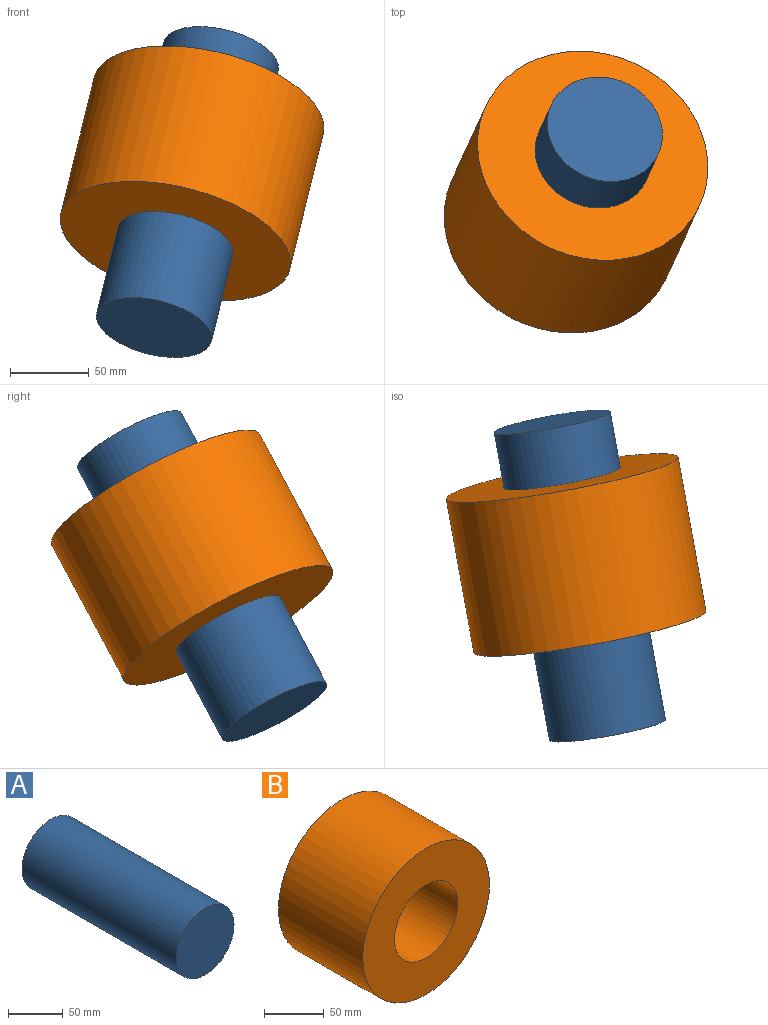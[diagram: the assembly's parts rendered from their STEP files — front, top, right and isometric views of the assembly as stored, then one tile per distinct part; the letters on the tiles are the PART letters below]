
ASSEMBLY  parts=2 mates=1
PART A: 3 faces, bbox 75x200x75 mm
  f0: cylinder r=37.5mm len=200mm, axis (0,1,0), area 47123.9mm2, adj f1,f2
  f1: plane 75x75mm, normal (0,-1,0), area 4417.9mm2, adj f0
  f2: plane 75x75mm, normal (0,1,0), area 4417.9mm2, adj f0
PART B: 4 faces, bbox 150x100x150 mm
  f0: cylinder r=75mm len=150mm, axis (0,1,0), area 47123.9mm2, adj f1,f2
  f1: plane 150x150mm, normal (0,-1,0), area 13253.6mm2, adj f0,f3
  f2: plane 150x150mm, normal (0,1,0), area 13253.6mm2, adj f0,f3
  f3: cylinder r=37.5mm len=100mm, axis (0,1,0), area 23561.9mm2, adj f1,f2
PLACE A rot(axis=(0.94,-0.14,-0.32),63.3deg) t=(9.34,4.48,127.31)mm fixed
PLACE B rot(axis=(0.24,0.85,0.47),157.3deg) t=(1.62,-12.28,95.99)mm
MATE cylindrical A.f0 <-> B.f0  axis (0.21,0.46,0.86) through (-11.89,-41.62,41.15)mm
